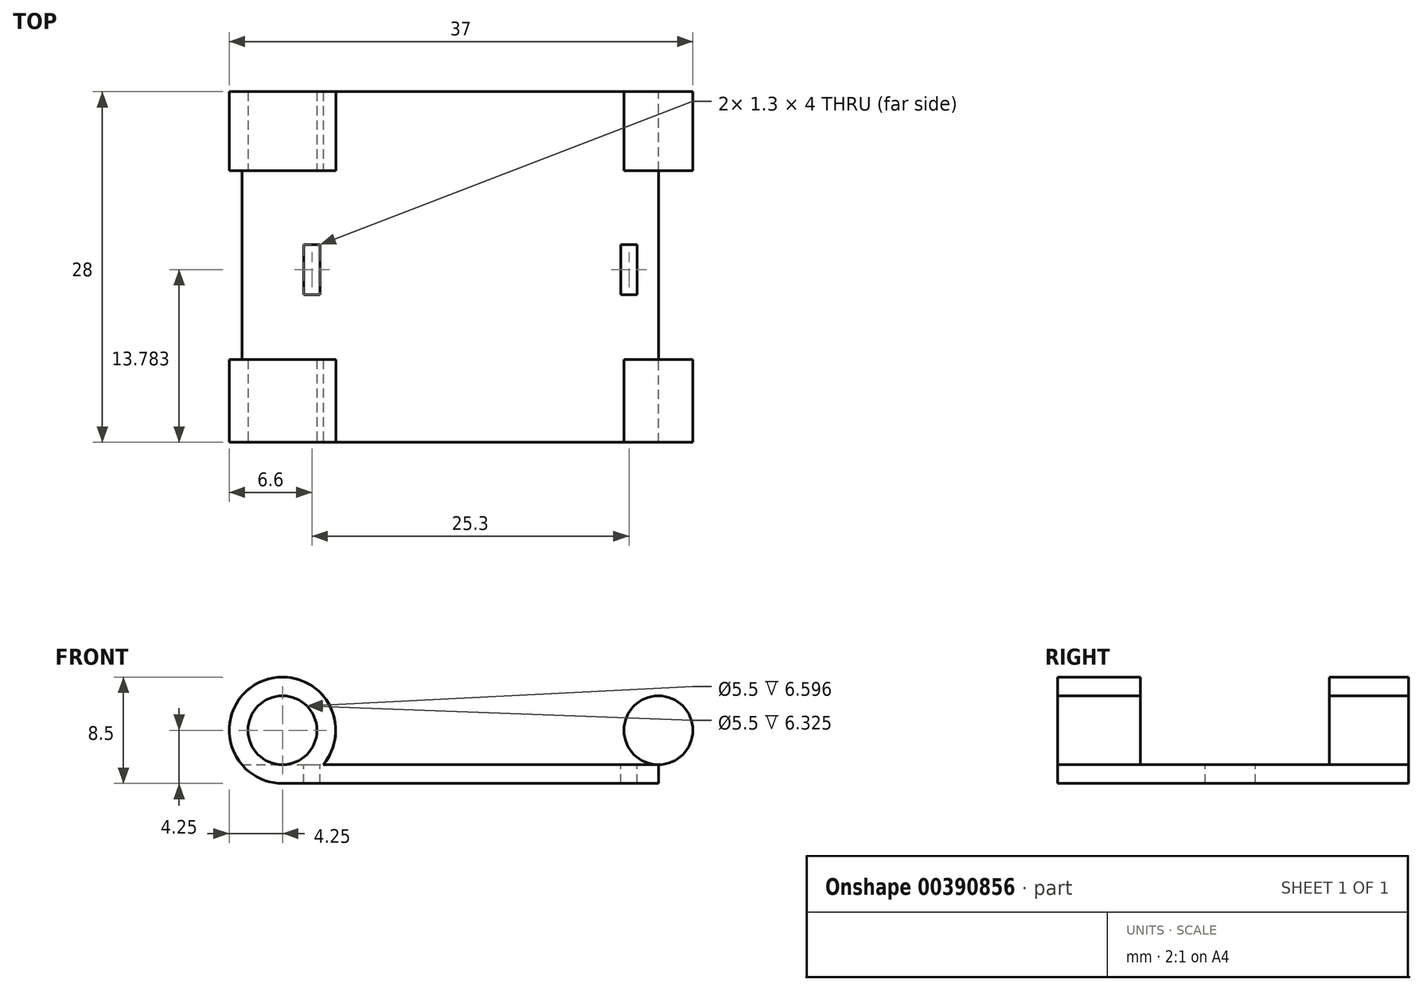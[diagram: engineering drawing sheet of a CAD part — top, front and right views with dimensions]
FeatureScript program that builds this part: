
annotation { "Feature Type Name" : "Feature", "Feature Type Description" : "" }
export const myFeature = defineFeature(function(context is Context, id is Id, definition is map)
    precondition{}
    {
        {
            var Q0;
            Q0=qCreatedBy(makeId("Top.planeOp"),FACE);
            var sketch = newSketch(context, id + "F0", { "sketchPlane" : qUnion([Q0])});
            skLineSegment(sketch, "E0.bottom", {"start": v(-15, -14) * mm, "end": v(15, -14) * mm});
            skLineSegment(sketch, "E0.top", {"start": v(-15, 14) * mm, "end": v(15, 14) * mm});
            skLineSegment(sketch, "E0.left", {"start": v(-15, -14) * mm, "end": v(-15, 14) * mm});
            skLineSegment(sketch, "E0.right", {"start": v(15, -14) * mm, "end": v(15, 14) * mm});
            skPoint(sketch, "E0.middle", {"position": v(0, 0) * mm});
            skSolve(sketch);
        }
        {
            var Q0;
            Q0 = qSketchRegion(id + "F0", true);
            extrude(context, id + "F1", {"entities" : qUnion([Q0]), "depth" : 1.5 * mm, "offsetDistance" : 25 * mm});
        }
        {
            var Q0;
            Q0=makeQuery(id+"F1.opExtrude","SWEPT_FACE",FACE,{"disambiguationData":[OSD([sQuery(id+"F0.wireOp",EDGE,"E0.bottom")])]});
            var sketch = newSketch(context, id + "F2", { "sketchPlane" : qUnion([Q0])});
            skCircle(sketch, "E1", {"center": v(-15, 4.25) * mm, "radius": 4.25 * mm});
            skCircle(sketch, "E2", {"center": v(-15, 4.25) * mm, "radius": 2.75 * mm});
            skCircle(sketch, "E3.MirrorC", {"center": v(15, 4.25) * mm, "radius": 4.25 * mm});
            skCircle(sketch, "E4.MirrorC", {"center": v(15, 4.25) * mm, "radius": 2.75 * mm});
            skSolve(sketch);
        }
        {
            var Q0;
            {var subQ5=sQuery(id+"F2.wireOp",EDGE,"E2");Q0=makeQuery(id+"F2.imprint","IMPRINT",FACE,{"disambiguationData":[TD([[makeQuery(id+"F2.imprint","IMPRINT",EDGE,{"derivedFrom":subQ5}),-1.0]])]});}
            var Q1;
            {var subQ5=sQuery(id+"F2.wireOp",EDGE,"E4.MirrorC");Q1=makeQuery(id+"F2.imprint","IMPRINT",FACE,{"disambiguationData":[TD([[makeQuery(id+"F2.imprint","IMPRINT",EDGE,{"derivedFrom":subQ5}),1.0]])]});}
            var Q2;
            {var subQ1=sQuery(id+"F0.wireOp",EDGE,"E0.bottom");var subQ2=makeQuery(id+"F1.opExtrude","SWEPT_EDGE",EDGE,{"disambiguationData":[OSD([subQ1,sQuery(id+"F0.wireOp",EDGE,"E0.right")])]});Q2=makeQuery(id+"F2.imprint","IMPRINT",FACE,{"disambiguationData":[TD([[makeQuery(id+"F2.imprint","IMPRINT",EDGE,{"derivedFrom":subQ2}),-1.0]])]});}
            var Q3;
            {var subQ1=sQuery(id+"F0.wireOp",EDGE,"E0.bottom");var subQ2=makeQuery(id+"F1.opExtrude","SWEPT_EDGE",EDGE,{"disambiguationData":[OSD([subQ1,sQuery(id+"F0.wireOp",EDGE,"E0.left")])]});Q3=makeQuery(id+"F2.imprint","IMPRINT",FACE,{"disambiguationData":[TD([[makeQuery(id+"F2.imprint","IMPRINT",EDGE,{"derivedFrom":subQ2}),1.0]])]});}
            extrude(context, id + "F3", {"entities" : qUnion([Q0, Q1, Q2, Q3]), "operationType" : NewBodyOperationType.ADD, "oppositeDirection" : true, "depth" : 28 * mm, "offsetDistance" : 25 * mm});
        }
        {
            var Q0;
            Q0=makeQuery(id+"F1.opExtrude","CAP_FACE",FACE,{"disambiguationData":[OSD([sQuery(id+"F0.wireOp",EDGE,"E0.bottom"),sQuery(id+"F0.wireOp",EDGE,"E0.top"),sQuery(id+"F0.wireOp",EDGE,"E0.left"),sQuery(id+"F0.wireOp",EDGE,"E0.right")])],"isStart":false});
            var sketch = newSketch(context, id + "F4", { "sketchPlane" : qUnion([Q0])});
            skLineSegment(sketch, "E5", {"start": v(0, 8.04) * mm, "end": v(0, -8.66) * mm, "construction": true});
            skLineSegment(sketch, "E6.bottom", {"start": v(-13.3, 1.78) * mm, "end": v(-12, 1.78) * mm});
            skLineSegment(sketch, "E6.top", {"start": v(-13.3, -2.22) * mm, "end": v(-12, -2.22) * mm});
            skLineSegment(sketch, "E6.left", {"start": v(-13.3, 1.78) * mm, "end": v(-13.3, -2.22) * mm});
            skLineSegment(sketch, "E6.right", {"start": v(-12, 1.78) * mm, "end": v(-12, -2.22) * mm});
            skLineSegment(sketch, "E7.MirrorCS", {"start": v(12, 1.78) * mm, "end": v(12, -2.22) * mm});
            skLineSegment(sketch, "E8.MirrorCS", {"start": v(13.3, 1.78) * mm, "end": v(12, 1.78) * mm});
            skLineSegment(sketch, "E9.MirrorCS", {"start": v(13.3, 1.78) * mm, "end": v(13.3, -2.22) * mm});
            skLineSegment(sketch, "E10.MirrorCS", {"start": v(13.3, -2.22) * mm, "end": v(12, -2.22) * mm});
            skSolve(sketch);
        }
        {
            var Q0;
            Q0=makeQuery(id+"F4.imprint","IMPRINT",FACE,{"disambiguationData":[TD([[makeQuery(id+"F4.imprint","IMPRINT",EDGE,{"derivedFrom":sQuery(id+"F4.wireOp",EDGE,"E6.bottom")}),-1.0]])]});
            var Q1;
            Q1=makeQuery(id+"F4.imprint","IMPRINT",FACE,{"disambiguationData":[TD([[makeQuery(id+"F4.imprint","IMPRINT",EDGE,{"derivedFrom":sQuery(id+"F4.wireOp",EDGE,"E7.MirrorCS")}),1.0]])]});
            extrude(context, id + "F5", {"entities" : qUnion([Q0, Q1]), "operationType" : NewBodyOperationType.REMOVE, "oppositeDirection" : true, "depth" : 25 * mm, "offsetDistance" : 25 * mm});
        }
        {
            var Q0;
            Q0=makeQuery(id+"F1.opExtrude","CAP_FACE",FACE,{"disambiguationData":[OSD([sQuery(id+"F0.wireOp",EDGE,"E0.bottom"),sQuery(id+"F0.wireOp",EDGE,"E0.top"),sQuery(id+"F0.wireOp",EDGE,"E0.left"),sQuery(id+"F0.wireOp",EDGE,"E0.right")])],"isStart":false});
            var sketch = newSketch(context, id + "F6", { "sketchPlane" : qUnion([Q0])});
            skLineSegment(sketch, "E11.bottom", {"start": v(-20.64, 7.68) * mm, "end": v(20.7, 7.68) * mm});
            skLineSegment(sketch, "E11.top", {"start": v(-20.64, -7.4) * mm, "end": v(20.7, -7.4) * mm});
            skLineSegment(sketch, "E11.left", {"start": v(-20.64, 7.68) * mm, "end": v(-20.64, -7.4) * mm});
            skLineSegment(sketch, "E11.right", {"start": v(20.7, 7.68) * mm, "end": v(20.7, -7.4) * mm});
            skSolve(sketch);
        }
        {
            var Q0;
            Q0 = qSketchRegion(id + "F6", true);
            extrude(context, id + "F7", {"entities" : qUnion([Q0]), "operationType" : NewBodyOperationType.REMOVE, "depth" : 25 * mm, "offsetDistance" : 25 * mm});
        }
    });
